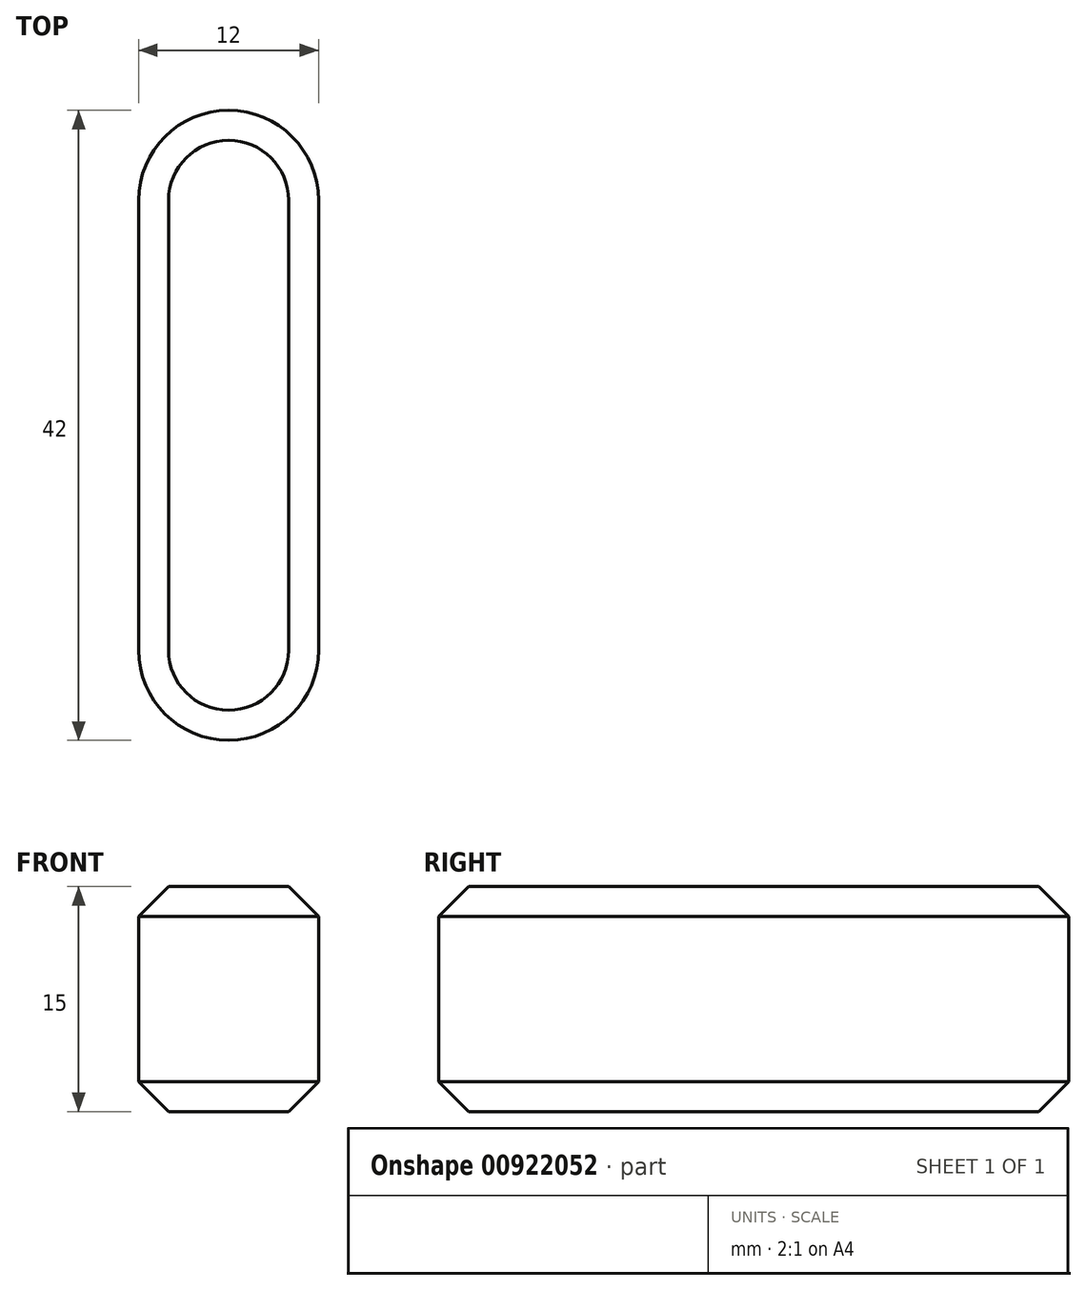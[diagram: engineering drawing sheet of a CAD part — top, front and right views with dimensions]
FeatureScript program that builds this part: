
annotation { "Feature Type Name" : "Feature", "Feature Type Description" : "" }
export const myFeature = defineFeature(function(context is Context, id is Id, definition is map)
    precondition{}
    {
        {
            var Q0;
            Q0=qCreatedBy(makeId("Top.planeOp"),FACE);
            var sketch = newSketch(context, id + "F0", { "sketchPlane" : qUnion([Q0])});
            skLineSegment(sketch, "E0.right", {"start": v(-6, 0) * mm, "end": v(-6, 15) * mm});
            skLineSegment(sketch, "E1.MirrorCS", {"start": v(6, 0) * mm, "end": v(6, 15) * mm});
            skLineSegment(sketch, "E2.MirrorCS", {"start": v(-6, 0) * mm, "end": v(-6, -15) * mm});
            skLineSegment(sketch, "E3.MirrorCS", {"start": v(6, 0) * mm, "end": v(6, -15) * mm});
            skArc(sketch, "E4", {"start": v(6, 15) * mm, "mid": v(0, 21) * mm, "end": v(-6, 15) * mm});
            skArc(sketch, "E5", {"start": v(-6, -15) * mm, "mid": v(0, -21) * mm, "end": v(6, -15) * mm});
            skSolve(sketch);
        }
        {
            var Q0;
            Q0 = qSketchRegion(id + "F0", true);
            extrude(context, id + "F1", {"entities" : qUnion([Q0]), "depth" : 15 * mm, "offsetDistance" : 25 * mm});
        }
        {
            var Q0;
            Q0=makeQuery(id+"F1.opExtrude","CAP_EDGE",EDGE,{"disambiguationData":[OSD([sQuery(id+"F0.wireOp",EDGE,"E1.MirrorCS"),sQuery(id+"F0.wireOp",EDGE,"E3.MirrorCS")])],"isStart":false});
            var Q1;
            Q1=makeQuery(id+"F1.opExtrude","CAP_EDGE",EDGE,{"disambiguationData":[OSD([sQuery(id+"F0.wireOp",EDGE,"E1.MirrorCS"),sQuery(id+"F0.wireOp",EDGE,"E3.MirrorCS")])],"isStart":true});
            chamfer(context, id + "F2", {"entities" : qUnion([Q0, Q1]), "width" : 2 * mm, "tangentPropagation" : true});
        }
    });
